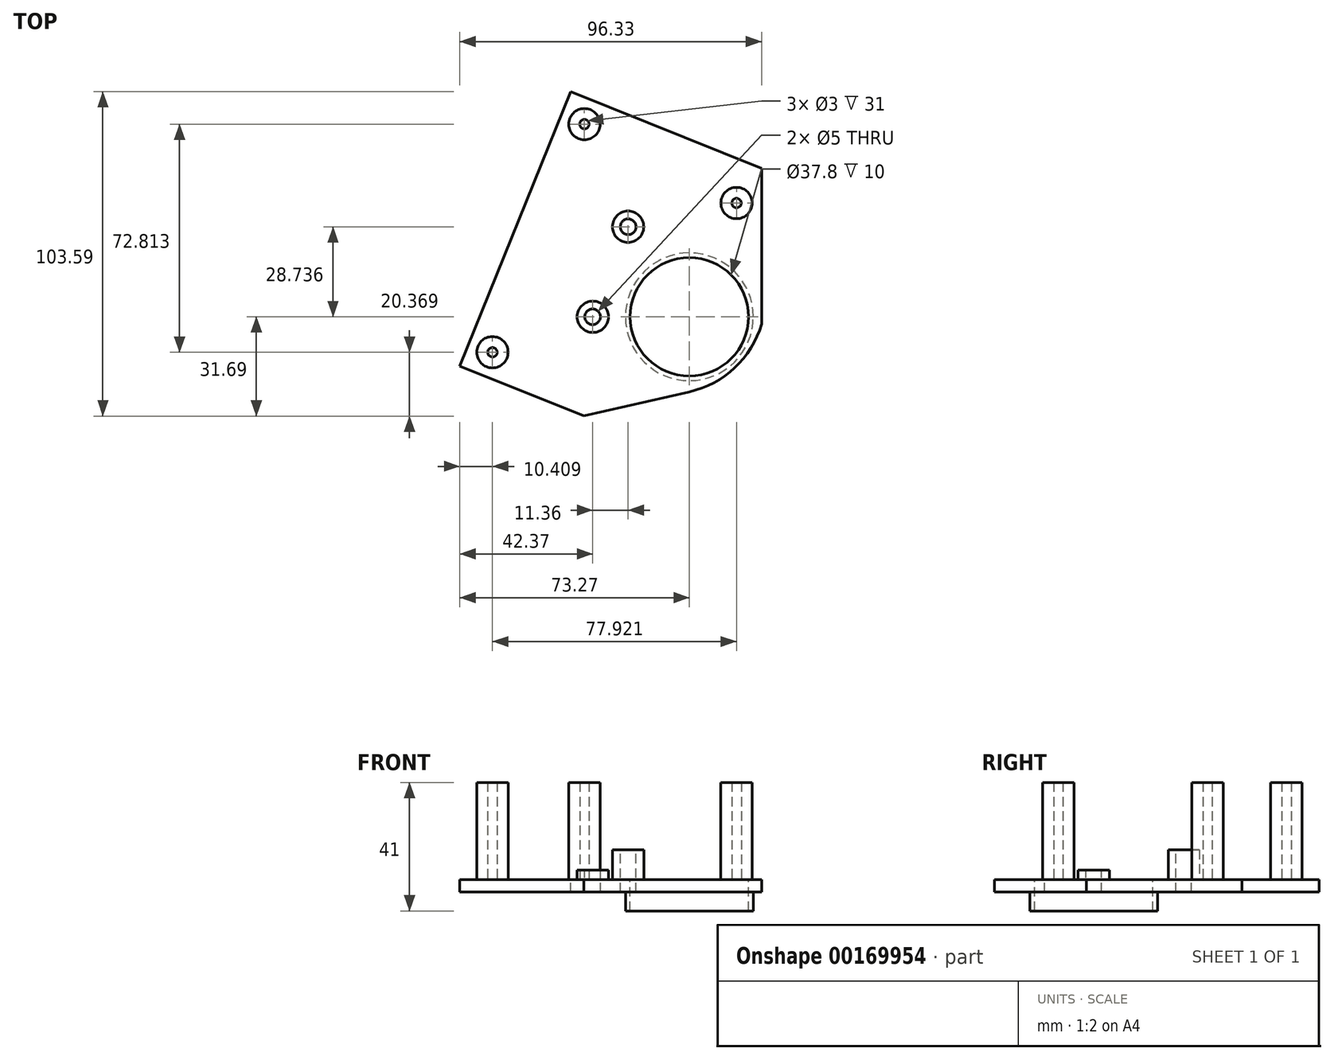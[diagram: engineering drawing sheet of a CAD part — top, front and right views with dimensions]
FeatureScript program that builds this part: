
annotation { "Feature Type Name" : "Feature", "Feature Type Description" : "" }
export const myFeature = defineFeature(function(context is Context, id is Id, definition is map)
    precondition{}
    {
        {
            var Q0;
            Q0=qCreatedBy(makeId("Top.planeOp"),FACE);
            var sketch = newSketch(context, id + "F0", { "sketchPlane" : qUnion([Q0])});
            skCircle(sketch, "E0", {"center": v(0, 0) * mm, "radius": 18.9 * mm});
            skCircle(sketch, "E1", {"center": v(0, 0) * mm, "radius": 20.4 * mm});
            skCircle(sketch, "E2", {"center": v(-30.9, 0) * mm, "radius": 2.5 * mm});
            skCircle(sketch, "E3", {"center": v(0, 0) * mm, "radius": 5.6 * mm, "construction": true});
            skCircle(sketch, "E4", {"center": v(-30.9, 0) * mm, "radius": 24.8 * mm, "construction": true});
            skCircle(sketch, "E5", {"center": v(-30.9, 0) * mm, "radius": 5.6 * mm, "construction": true});
            skCircle(sketch, "E6", {"center": v(-19.54, 28.74) * mm, "radius": 24.8 * mm, "construction": true});
            skCircle(sketch, "E7", {"center": v(-19.54, 28.74) * mm, "radius": 2.5 * mm});
            skLineSegment(sketch, "E8", {"start": v(-73.27, -15.75) * mm, "end": v(-37.94, 71.9) * mm});
            skLineSegment(sketch, "E9", {"start": v(-37.94, 71.9) * mm, "end": v(23.06, 47.31) * mm});
            skLineSegment(sketch, "E10", {"start": v(23.06, 47.31) * mm, "end": v(23.06, -2.33) * mm});
            skLineSegment(sketch, "E11", {"start": v(-73.27, -15.75) * mm, "end": v(-33.74, -31.69) * mm});
            skLineSegment(sketch, "E12", {"start": v(-33.74, -31.69) * mm, "end": v(0, -23.97) * mm});
            skArc(sketch, "E13", {"start": v(0, -23.97) * mm, "mid": v(14.46, -16.27) * mm, "end": v(23.06, -2.33) * mm});
            skCircle(sketch, "E14", {"center": v(0, 0) * mm, "radius": 6.5 * mm});
            skLineSegment(sketch, "E15", {"start": v(0, 0) * mm, "end": v(9.83, 20.34) * mm, "construction": true});
            skLineSegment(sketch, "E16", {"start": v(9.83, 20.34) * mm, "end": v(-10.98, -23.06) * mm, "construction": true});
            skCircle(sketch, "E17", {"center": v(-5.34, -11.3) * mm, "radius": 1.5 * mm});
            skCircle(sketch, "E18", {"center": v(5.44, 11.25) * mm, "radius": 1.5 * mm});
            skSolve(sketch);
        }
        {
            var Q0;
            Q0=makeQuery(id+"F0.imprint","IMPRINT",FACE,{"disambiguationData":[TD([[makeQuery(id+"F0.imprint","IMPRINT",EDGE,{"derivedFrom":sQuery(id+"F0.wireOp",EDGE,"E0")}),-1.0]])]});
            extrude(context, id + "F1", {"entities" : qUnion([Q0]), "oppositeDirection" : true, "depth" : 10 * mm});
        }
        {
            var Q0;
            Q0 = qSketchRegion(id + "F0", true);
            extrude(context, id + "F2", {"entities" : qUnion([Q0]), "operationType" : NewBodyOperationType.ADD, "oppositeDirection" : true, "depth" : 4 * mm});
        }
        {
            var Q0;
            Q0=makeQuery(id+"F0.imprint","IMPRINT",FACE,{"disambiguationData":[TD([[makeQuery(id+"F0.imprint","IMPRINT",EDGE,{"derivedFrom":sQuery(id+"F0.wireOp",EDGE,"E1")}),-1.0]])]});
            var sketch = newSketch(context, id + "F3", { "sketchPlane" : qUnion([Q0])});
            skCircle(sketch, "E19", {"center": v(-30.82, 0) * mm, "radius": 5 * mm});
            skCircle(sketch, "E20", {"center": v(-19.57, 28.75) * mm, "radius": 5 * mm});
            skCircle(sketch, "E21", {"center": v(15.06, 36.31) * mm, "radius": 5 * mm});
            skCircle(sketch, "E22", {"center": v(15.06, 36.31) * mm, "radius": 1.5 * mm});
            skCircle(sketch, "E23", {"center": v(-33.5, 61.5) * mm, "radius": 5 * mm});
            skCircle(sketch, "E24", {"center": v(-33.5, 61.5) * mm, "radius": 1.5 * mm});
            skCircle(sketch, "E25", {"center": v(-62.86, -11.32) * mm, "radius": 5 * mm});
            skCircle(sketch, "E26", {"center": v(-62.86, -11.32) * mm, "radius": 1.5 * mm});
            skSolve(sketch);
        }
        {
            var Q0;
            Q0=makeQuery(id+"F3.imprint","IMPRINT",FACE,{"disambiguationData":[TD([[makeQuery(id+"F3.imprint","IMPRINT",EDGE,{"derivedFrom":sQuery(id+"F3.wireOp",EDGE,"E19")}),1.0]])]});
            var Q1;
            Q1=sQuery(id+"F3.wireOp",EDGE,"E19");
            extrude(context, id + "F4", {"entities" : qUnion([Q0]), "operationType" : NewBodyOperationType.ADD, "surfaceEntities" : qUnion([Q1]), "depth" : 3 * mm});
        }
        {
            var Q0;
            Q0=makeQuery(id+"F3.imprint","IMPRINT",FACE,{"disambiguationData":[TD([[makeQuery(id+"F3.imprint","IMPRINT",EDGE,{"derivedFrom":sQuery(id+"F3.wireOp",EDGE,"E20")}),1.0]])]});
            extrude(context, id + "F5", {"entities" : qUnion([Q0]), "operationType" : NewBodyOperationType.ADD, "depth" : 9.5 * mm});
        }
        {
            var Q0;
            Q0=makeQuery(id+"F3.imprint","IMPRINT",FACE,{"disambiguationData":[TD([[makeQuery(id+"F3.imprint","IMPRINT",EDGE,{"derivedFrom":sQuery(id+"F3.wireOp",EDGE,"E21")}),1.0]])]});
            var Q1;
            Q1=makeQuery(id+"F3.imprint","IMPRINT",FACE,{"disambiguationData":[TD([[makeQuery(id+"F3.imprint","IMPRINT",EDGE,{"derivedFrom":sQuery(id+"F3.wireOp",EDGE,"E23")}),1.0]])]});
            var Q2;
            Q2=makeQuery(id+"F3.imprint","IMPRINT",FACE,{"disambiguationData":[TD([[makeQuery(id+"F3.imprint","IMPRINT",EDGE,{"derivedFrom":sQuery(id+"F3.wireOp",EDGE,"E25")}),1.0]])]});
            extrude(context, id + "F6", {"entities" : qUnion([Q0, Q1, Q2]), "operationType" : NewBodyOperationType.ADD, "depth" : 31 * mm});
        }
    });
